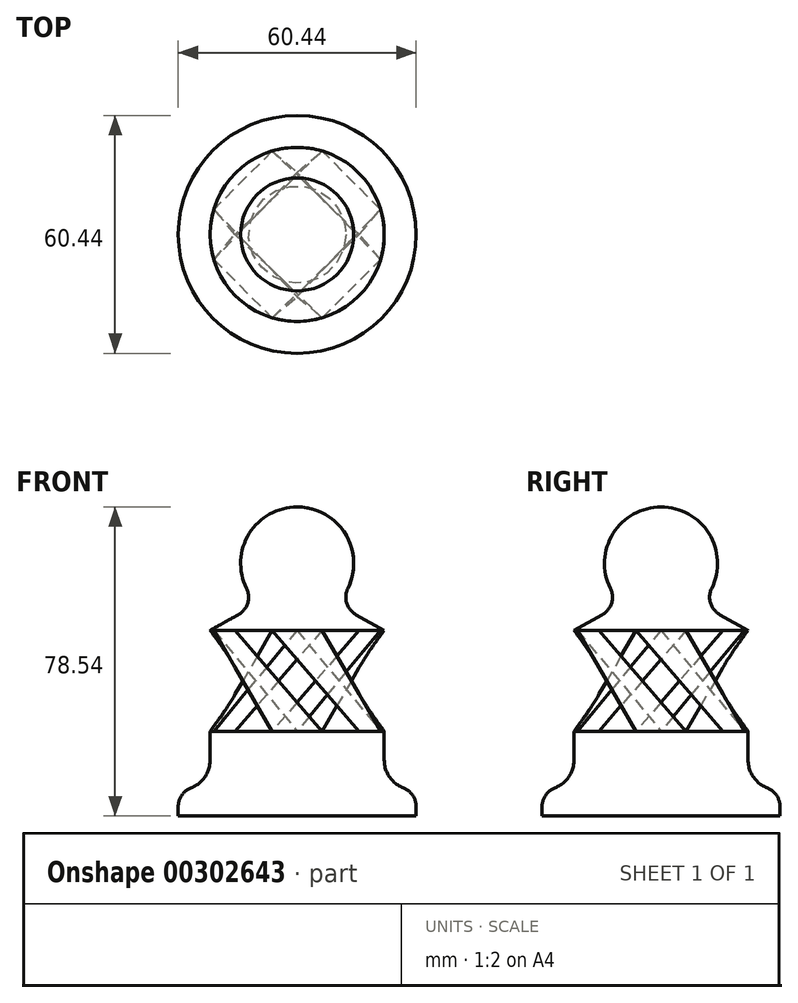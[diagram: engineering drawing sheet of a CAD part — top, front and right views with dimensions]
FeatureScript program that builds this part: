
annotation { "Feature Type Name" : "Feature", "Feature Type Description" : "" }
export const myFeature = defineFeature(function(context is Context, id is Id, definition is map)
    precondition{}
    {
        {
            var Q0;
            Q0=qCreatedBy(makeId("Front.planeOp"),FACE);
            var sketch = newSketch(context, id + "F0", { "sketchPlane" : qUnion([Q0])});
            skLineSegment(sketch, "E0", {"start": v(0, 0) * mm, "end": v(-30.22, 0) * mm});
            skLineSegment(sketch, "E1", {"start": v(-30.22, 0) * mm, "end": v(-30.22, 6.62) * mm});
            skLineSegment(sketch, "E2", {"start": v(-30.22, 6.62) * mm, "end": v(-22.11, 6.62) * mm});
            skLineSegment(sketch, "E3", {"start": v(-22.11, 6.62) * mm, "end": v(-22.11, 21.54) * mm});
            skLineSegment(sketch, "E4", {"start": v(-22.11, 21.54) * mm, "end": v(0, 21.54) * mm});
            skLineSegment(sketch, "E5", {"start": v(0, 21.54) * mm, "end": v(0, 0) * mm});
            skLineSegment(sketch, "E6", {"start": v(0, 47.18) * mm, "end": v(-22.11, 47.18) * mm});
            skLineSegment(sketch, "E7", {"start": v(-22.11, 47.18) * mm, "end": v(-10, 53.9) * mm});
            skArc(sketch, "E8", {"start": v(0, 78.54) * mm, "mid": v(-13.3, 69.58) * mm, "end": v(-10, 53.9) * mm});
            skLineSegment(sketch, "E9", {"start": v(0, 47.18) * mm, "end": v(0, 78.54) * mm});
            skSolve(sketch);
        }
        {
            var Q0;
            Q0 = qSketchRegion(id + "F0", true);
            var Q1;
            Q1=sQuery(id+"F0.wireOp",EDGE,"E9");
            revolve(context, id + "F1", {"entities" : qUnion([Q0]), "axis" : qUnion([Q1]), "revolveType" : RevolveType.FULL});
        }
        {
            var Q0;
            Q0=makeQuery(id+"F1.opRevolve","SWEPT_FACE",FACE,{"disambiguationData":[OSD([sQuery(id+"F0.wireOp",EDGE,"E4")])]});
            var sketch = newSketch(context, id + "F2", { "sketchPlane" : qUnion([Q0])});
            skArc(sketch, "E10.0", {"start": v(-6.35, -21.18) * mm, "mid": v(0, -22.11) * mm, "end": v(6.35, -21.18) * mm});
            skLineSegment(sketch, "E11", {"start": v(-6.35, -21.18) * mm, "end": v(0, -15.76) * mm});
            skLineSegment(sketch, "E12", {"start": v(0, -15.76) * mm, "end": v(6.35, -21.18) * mm});
            skSolve(sketch);
        }
        {
            var Q0;
            Q0=makeQuery(id+"F1.opRevolve","SWEPT_FACE",FACE,{"disambiguationData":[OSD([sQuery(id+"F0.wireOp",EDGE,"E6")])]});
            var sketch = newSketch(context, id + "F3", { "sketchPlane" : qUnion([Q0])});
            skArc(sketch, "E13.0", {"start": v(-21.18, 6.35) * mm, "mid": v(-22.11, 0) * mm, "end": v(-21.18, -6.35) * mm});
            skLineSegment(sketch, "E14", {"start": v(-21.18, 6.35) * mm, "end": v(-15.76, 0) * mm});
            skLineSegment(sketch, "E15", {"start": v(-15.76, 0) * mm, "end": v(-21.18, -6.35) * mm});
            skLineSegment(sketch, "E16", {"start": v(-6.35, 21.18) * mm, "end": v(6.35, 21.18) * mm, "construction": true});
            skLineSegment(sketch, "E17", {"start": v(-21.18, 6.35) * mm, "end": v(-21.18, -6.35) * mm, "construction": true});
            skSolve(sketch);
        }
        {
            var Q0;
            Q0=makeQuery(id+"F3.imprint","IMPRINT",FACE,{"disambiguationData":[TD([[makeQuery(id+"F3.imprint","IMPRINT",EDGE,{"derivedFrom":sQuery(id+"F3.wireOp",EDGE,"E13.0")}),1.0]])]});
            var Q1;
            Q1=makeQuery(id+"F2.imprint","IMPRINT",FACE,{"disambiguationData":[TD([[makeQuery(id+"F2.imprint","IMPRINT",EDGE,{"derivedFrom":sQuery(id+"F2.wireOp",EDGE,"E10.0")}),-1.0]])]});
            loft(context, id + "F4", {"sheetProfilesArray" : [{ "sheetProfileEntities" : qUnion([Q0]) }, { "sheetProfileEntities" : qUnion([Q1]) }]});
        }
        {
            var Q0;
            Q0=makeQuery(id+"F4.opLoft","SWEPT_BODY",BODY,{"disambiguationData":[OSD([makeQuery(id+"F2.imprint","IMPRINT",FACE,{"disambiguationData":[TD([[makeQuery(id+"F2.imprint","IMPRINT",EDGE,{"derivedFrom":sQuery(id+"F2.wireOp",EDGE,"E10.0")}),-1.0]])]}),makeQuery(id+"F3.imprint","IMPRINT",FACE,{"disambiguationData":[TD([[makeQuery(id+"F3.imprint","IMPRINT",EDGE,{"derivedFrom":sQuery(id+"F3.wireOp",EDGE,"E13.0")}),1.0]])]})])]});
            var Q1;
            Q1=makeQuery(id+"F1.opRevolve","SWEPT_EDGE",EDGE,{"disambiguationData":[OSD([sQuery(id+"F0.wireOp",EDGE,"E3"),sQuery(id+"F0.wireOp",EDGE,"E4")])]});
            circularPattern(context, id + "F5", {"entities" : qUnion([Q0]), "axis" : qUnion([Q1]), "angle" : 360 * degree, "instanceCount" : 4, "equalSpace" : true});
        }
        {
            var Q0;
            Q0=makeQuery(id+"F1.opRevolve","SWEPT_EDGE",EDGE,{"disambiguationData":[OSD([sQuery(id+"F0.wireOp",EDGE,"E2"),sQuery(id+"F0.wireOp",EDGE,"E3")])]});
            fillet(context, id + "F6", {"entities" : qUnion([Q0]), "radius" : 7.62 * mm, "tangentPropagation" : true, "allowEdgeOverflow" : false});
        }
        {
            var Q0;
            Q0=makeQuery(id+"F1.opRevolve","SWEPT_EDGE",EDGE,{"disambiguationData":[OSD([sQuery(id+"F0.wireOp",EDGE,"E1"),sQuery(id+"F0.wireOp",EDGE,"E2")])]});
            fillet(context, id + "F7", {"entities" : qUnion([Q0]), "radius" : 5.08 * mm, "tangentPropagation" : true, "allowEdgeOverflow" : false});
        }
        {
            var Q0;
            Q0=makeQuery(id+"F1.opRevolve","SWEPT_EDGE",EDGE,{"disambiguationData":[OSD([sQuery(id+"F0.wireOp",EDGE,"E7"),sQuery(id+"F0.wireOp",EDGE,"E8")])]});
            fillet(context, id + "F8", {"entities" : qUnion([Q0]), "radius" : 5.08 * mm, "tangentPropagation" : true, "allowEdgeOverflow" : false});
        }
    });
